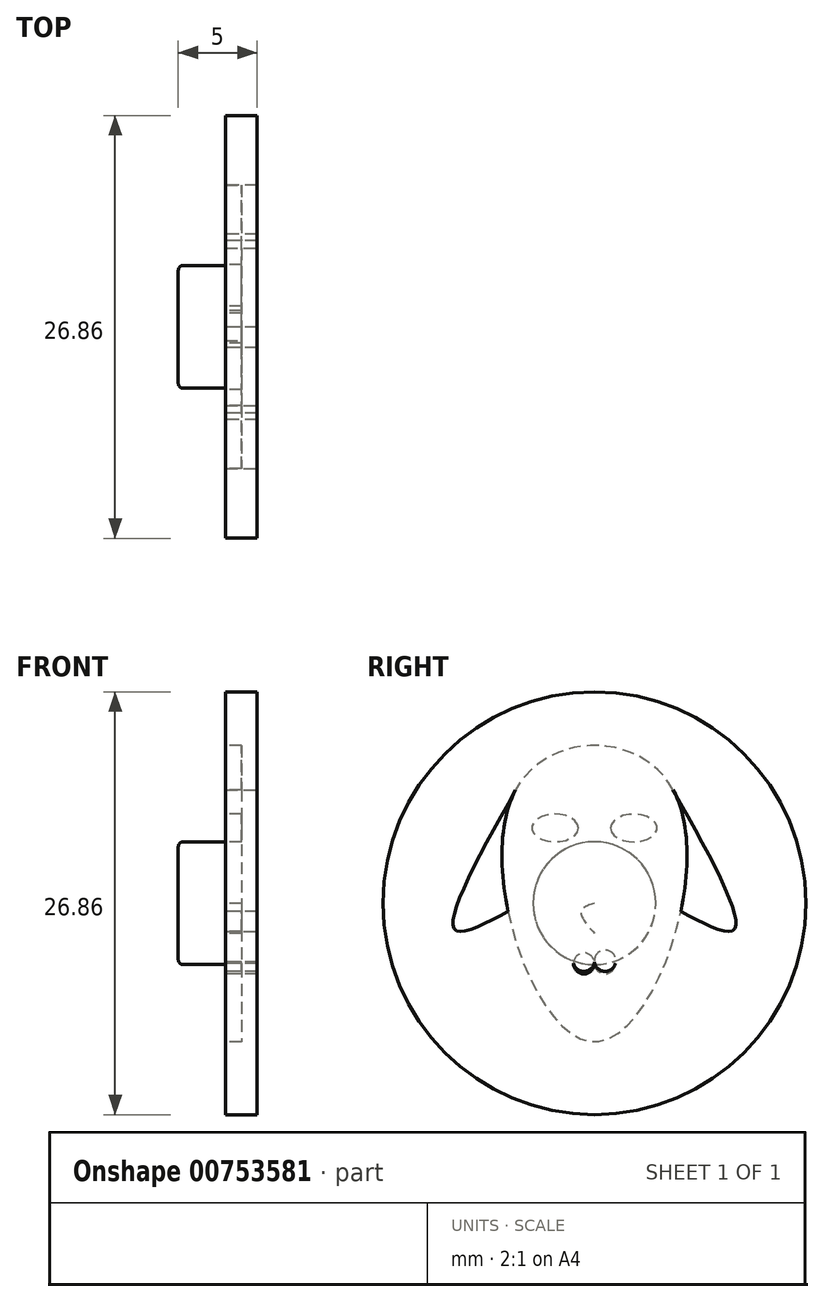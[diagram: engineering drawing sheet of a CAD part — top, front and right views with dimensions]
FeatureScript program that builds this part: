
annotation { "Feature Type Name" : "Feature", "Feature Type Description" : "" }
export const myFeature = defineFeature(function(context is Context, id is Id, definition is map)
    precondition{}
    {
        {
            var Q0;
            Q0=qCreatedBy(makeId("Right.planeOp"),FACE);
            var sketch = newSketch(context, id + "F0", { "sketchPlane" : qUnion([Q0])});
            skFitSpline(sketch, "E0", {"points": [v(-5, 16) * mm, v(0, 0) * mm, v(5, 16) * mm, v(-5, 16) * mm]});
            skEllipse(sketch, "E1", {"center": v(-2.5, 13.58) * mm, "majorRadius": 1.47 * mm, "minorRadius": 0.88 * mm, "majorAxis": v(1, 0)});
            skEllipse(sketch, "E2.MirrorC", {"center": v(2.5, 13.58) * mm, "majorRadius": 1.47 * mm, "minorRadius": 0.88 * mm, "majorAxis": v(-1, 0)});
            skFitSpline(sketch, "E3", {"points": [v(0, 8.8) * mm, v(-0.86, 8.3) * mm, v(0, 6.87) * mm], "startDerivative": vector(-2.73, -0.86) * mm, "endDerivative": vector(2.5, -2.91) * mm});
            skFitSpline(sketch, "E4.MirrorCS", {"points": [v(0, 8.8) * mm, v(0.86, 8.3) * mm, v(0, 6.87) * mm], "startDerivative": vector(2.73, -0.86) * mm, "endDerivative": vector(-2.5, -2.91) * mm});
            skLineSegment(sketch, "E5", {"start": v(0, 6.87) * mm, "end": v(0, 4.98) * mm});
            skArc(sketch, "E6", {"start": v(0, 4.98) * mm, "mid": v(0.67, 4.31) * mm, "end": v(1.33, 4.98) * mm});
            skArc(sketch, "E7.MirrorCS", {"start": v(0, 4.98) * mm, "mid": v(-0.67, 4.31) * mm, "end": v(-1.33, 4.98) * mm});
            skPoint(sketch, "E8", {"position": v(-8.88, 7.13) * mm});
            skFitSpline(sketch, "E9", {"points": [v(-5, 16) * mm, v(-8.88, 7.13) * mm, v(-5.49, 8.28) * mm], "startDerivative": vector(-10.97, -19.64) * mm, "endDerivative": vector(11.88, 6.3) * mm});
            skFitSpline(sketch, "E10.MirrorCS", {"points": [v(5, 16) * mm, v(8.88, 7.13) * mm, v(5.49, 8.28) * mm], "startDerivative": vector(10.97, -19.64) * mm, "endDerivative": vector(-11.88, 6.3) * mm});
            skLineSegment(sketch, "E11", {"start": v(0, 0) * mm, "end": v(0, 18.81) * mm, "construction": true});
            skPoint(sketch, "E12", {"position": v(0, 22.23) * mm});
            skCircle(sketch, "E13", {"center": v(0, 8.8) * mm, "radius": 13.43 * mm});
            skArc(sketch, "E14", {"start": v(-1.33, 4.98) * mm, "mid": v(-0.62, 4.47) * mm, "end": v(0, 5.07) * mm});
            skArc(sketch, "E15.MirrorCS", {"start": v(1.33, 4.98) * mm, "mid": v(0.62, 4.47) * mm, "end": v(0, 5.07) * mm});
            skSolve(sketch);
        }
        {
            var Q0;
            {var subQ1=sQuery(id+"F0.wireOp",EDGE,"E9");Q0=makeQuery(id+"F0.imprint","IMPRINT",FACE,{"disambiguationData":[TD([[makeQuery(id+"F0.imprint","IMPRINT",EDGE,{"derivedFrom":subQ1}),-1.0]])]});}
            var Q1;
            Q1=makeQuery(id+"F0.imprint","IMPRINT",FACE,{"disambiguationData":[TD([[makeQuery(id+"F0.imprint","IMPRINT",EDGE,{"derivedFrom":sQuery(id+"F0.wireOp",EDGE,"E3")}),1.0]])]});
            var Q2;
            Q2=makeQuery(id+"F0.imprint","IMPRINT",FACE,{"disambiguationData":[TD([[makeQuery(id+"F0.imprint","IMPRINT",EDGE,{"derivedFrom":sQuery(id+"F0.wireOp",EDGE,"E2.MirrorC")}),1.0]])]});
            var Q3;
            Q3=makeQuery(id+"F0.imprint","IMPRINT",FACE,{"disambiguationData":[TD([[makeQuery(id+"F0.imprint","IMPRINT",EDGE,{"derivedFrom":sQuery(id+"F0.wireOp",EDGE,"E1")}),1.0]])]});
            var Q4;
            {var subQ0=sQuery(id+"F0.wireOp",EDGE,"E6");Q4=makeQuery(id+"F0.imprint","IMPRINT",FACE,{"disambiguationData":[TD([[makeQuery(id+"F0.imprint","IMPRINT",EDGE,{"derivedFrom":subQ0}),1.0]])]});}
            var Q5;
            {var subQ0=sQuery(id+"F0.wireOp",EDGE,"E7.MirrorCS");Q5=makeQuery(id+"F0.imprint","IMPRINT",FACE,{"disambiguationData":[TD([[makeQuery(id+"F0.imprint","IMPRINT",EDGE,{"derivedFrom":subQ0}),-1.0]])]});}
            extrude(context, id + "F1", {"entities" : qUnion([Q0, Q1, Q2, Q3, Q4, Q5]), "depth" : 2 * mm, "offsetDistance" : 25.4 * mm});
        }
        {
            var Q0;
            {var subQ0=sQuery(id+"F0.wireOp",EDGE,"E9");Q0=makeQuery(id+"F0.imprint","IMPRINT",FACE,{"disambiguationData":[TD([[makeQuery(id+"F0.imprint","IMPRINT",EDGE,{"derivedFrom":subQ0}),1.0]])]});}
            var Q1;
            Q1=makeQuery(id+"F0.imprint","IMPRINT",FACE,{"disambiguationData":[TD([[makeQuery(id+"F0.imprint","IMPRINT",EDGE,{"derivedFrom":sQuery(id+"F0.wireOp",EDGE,"E1")}),-1.0]])]});
            var Q2;
            {var subQ0=sQuery(id+"F0.wireOp",EDGE,"E10.MirrorCS");Q2=makeQuery(id+"F0.imprint","IMPRINT",FACE,{"disambiguationData":[TD([[makeQuery(id+"F0.imprint","IMPRINT",EDGE,{"derivedFrom":subQ0}),-1.0]])]});}
            extrude(context, id + "F2", {"entities" : qUnion([Q0, Q1, Q2]), "depth" : 1 * mm, "offsetDistance" : 25.4 * mm});
        }
        {
            var Q0;
            Q0=qCreatedBy(makeId("Right.planeOp"),FACE);
            var sketch = newSketch(context, id + "F3", { "sketchPlane" : qUnion([Q0])});
            skCircle(sketch, "E16", {"center": v(0, 8.8) * mm, "radius": 3.9 * mm});
            skSolve(sketch);
        }
        {
            var Q0;
            Q0 = qSketchRegion(id + "F3", true);
            extrude(context, id + "F4", {"entities" : qUnion([Q0]), "depth" : -3 * mm, "offsetDistance" : 25.4 * mm});
        }
        {
            var Q0;
            {var subQ0=sQuery(id+"F0.wireOp",EDGE,"E0");Q0=makeQuery(id+"F1.opExtrude","CAP_EDGE",EDGE,{"disambiguationData":[OSD([subQ0]),TDD([makeQuery(id+"F0.imprint","IMPRINT",EDGE,{"disambiguationData":[TD([[makeQuery(id+"F0.imprint","INTERSECT",VERTEX,{"disambiguationData":[OD(0.0)],"derivedFrom":[subQ0,sQuery(id+"F0.wireOp",EDGE,"E9")]}),1.0]])],"derivedFrom":subQ0})])],"isStart":false});}
            var Q1;
            Q1=makeQuery(id+"F1.opExtrude","CAP_EDGE",EDGE,{"disambiguationData":[OSD([sQuery(id+"F0.wireOp",EDGE,"E13")])],"isStart":false});
            var Q2;
            Q2=makeQuery(id+"F1.opExtrude","CAP_EDGE",EDGE,{"disambiguationData":[OSD([sQuery(id+"F0.wireOp",EDGE,"E13")])],"isStart":true});
            var Q3;
            Q3=makeQuery(id+"F4.opExtrude","CAP_EDGE",EDGE,{"disambiguationData":[OSD([sQuery(id+"F3.wireOp",EDGE,"E16")])],"isStart":false});
            var Q4;
            Q4=makeQuery(id+"F1.opExtrude","CAP_EDGE",EDGE,{"disambiguationData":[OSD([sQuery(id+"F0.wireOp",EDGE,"E9")])],"isStart":false});
            var Q5;
            {var subQ0=sQuery(id+"F0.wireOp",EDGE,"E0");Q5=makeQuery(id+"F1.opExtrude","CAP_EDGE",EDGE,{"disambiguationData":[OSD([subQ0]),TDD([makeQuery(id+"F0.imprint","IMPRINT",EDGE,{"disambiguationData":[TD([[makeQuery(id+"F0.imprint","INTERSECT",VERTEX,{"disambiguationData":[OD(1.0)],"derivedFrom":[subQ0,sQuery(id+"F0.wireOp",EDGE,"E9")]}),-1.0]])],"derivedFrom":subQ0})])],"isStart":false});}
            var Q6;
            Q6=makeQuery(id+"F1.opExtrude","CAP_EDGE",EDGE,{"disambiguationData":[OSD([sQuery(id+"F0.wireOp",EDGE,"E10.MirrorCS")])],"isStart":false});
            var Q7;
            Q7=makeQuery(id+"F1.opExtrude","CAP_EDGE",EDGE,{"disambiguationData":[OSD([sQuery(id+"F0.wireOp",EDGE,"E3")])],"isStart":false});
            var Q8;
            Q8=makeQuery(id+"F1.opExtrude","CAP_EDGE",EDGE,{"disambiguationData":[OSD([sQuery(id+"F0.wireOp",EDGE,"E4.MirrorCS")])],"isStart":false});
            var Q9;
            Q9=makeQuery(id+"F1.opExtrude","CAP_EDGE",EDGE,{"disambiguationData":[OSD([sQuery(id+"F0.wireOp",EDGE,"E1")])],"isStart":false});
            var Q10;
            Q10=makeQuery(id+"F1.opExtrude","CAP_EDGE",EDGE,{"disambiguationData":[OSD([sQuery(id+"F0.wireOp",EDGE,"E2.MirrorC")])],"isStart":false});
            fillet(context, id + "F5", {"entities" : qUnion([Q0, Q1, Q2, Q3, Q4, Q5, Q6, Q7, Q8, Q9, Q10]), "radius" : 0.3 * mm, "tangentPropagation" : true, "allowEdgeOverflow" : false});
        }
    });
